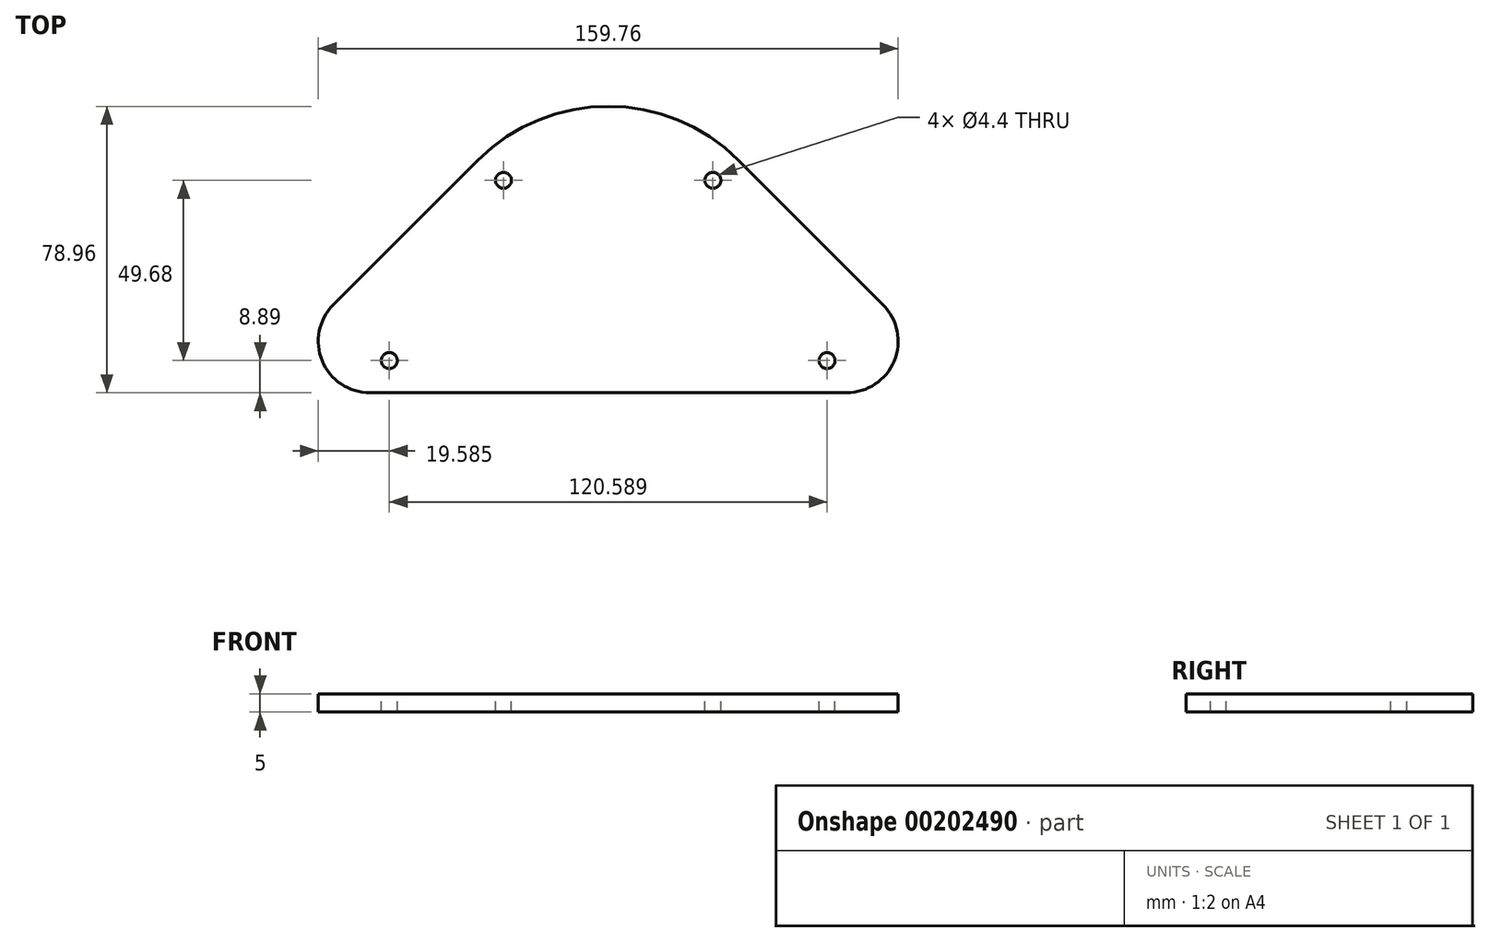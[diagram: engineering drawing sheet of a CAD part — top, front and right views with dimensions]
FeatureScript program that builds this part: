
annotation { "Feature Type Name" : "Feature", "Feature Type Description" : "" }
export const myFeature = defineFeature(function(context is Context, id is Id, definition is map)
    precondition{}
    {
        {
            var Q0;
            Q0=qCreatedBy(makeId("Top.planeOp"),FACE);
            var sketch = newSketch(context, id + "F0", { "sketchPlane" : qUnion([Q0])});
            skLineSegment(sketch, "E0", {"start": v(-100, 0) * mm, "end": v(0, 100) * mm});
            skLineSegment(sketch, "E1", {"start": v(0, 100) * mm, "end": v(100, 0) * mm});
            skLineSegment(sketch, "E2", {"start": v(100, 0) * mm, "end": v(-100, 0) * mm});
            skSolve(sketch);
        }
        {
            var Q0;
            Q0 = qSketchRegion(id + "F0", true);
            extrude(context, id + "F1", {"entities" : qUnion([Q0]), "depth" : 5 * mm});
        }
        {
            var Q0;
            Q0=makeQuery(id+"F1.opExtrude","SWEPT_EDGE",EDGE,{"disambiguationData":[OSD([sQuery(id+"F0.wireOp",EDGE,"E0"),sQuery(id+"F0.wireOp",EDGE,"E1")])]});
            fillet(context, id + "F2", {"entities" : qUnion([Q0]), "radius" : 50.8 * mm, "tangentPropagation" : true, "allowEdgeOverflow" : false});
        }
        {
            var Q0;
            Q0=makeQuery(id+"F1.opExtrude","SWEPT_EDGE",EDGE,{"disambiguationData":[OSD([sQuery(id+"F0.wireOp",EDGE,"E0"),sQuery(id+"F0.wireOp",EDGE,"E2")])]});
            var Q1;
            Q1=makeQuery(id+"F1.opExtrude","SWEPT_EDGE",EDGE,{"disambiguationData":[OSD([sQuery(id+"F0.wireOp",EDGE,"E1"),sQuery(id+"F0.wireOp",EDGE,"E2")])]});
            fillet(context, id + "F3", {"entities" : qUnion([Q0, Q1]), "radius" : 14.22 * mm, "tangentPropagation" : true, "allowEdgeOverflow" : false});
        }
        {
            var Q0;
            Q0=makeQuery(id+"F1.opExtrude","CAP_FACE",FACE,{"disambiguationData":[OSD([sQuery(id+"F0.wireOp",EDGE,"E0"),sQuery(id+"F0.wireOp",EDGE,"E1"),sQuery(id+"F0.wireOp",EDGE,"E2")])],"isStart":false});
            var sketch = newSketch(context, id + "F4", { "sketchPlane" : qUnion([Q0])});
            skLineSegment(sketch, "E3", {"start": v(-60.3, 8.89) * mm, "end": v(60.3, 8.89) * mm, "construction": true});
            skLineSegment(sketch, "E4", {"start": v(-28.86, 58.57) * mm, "end": v(28.86, 58.57) * mm, "construction": true});
            skPoint(sketch, "E5", {"position": v(0, 8.89) * mm});
            skPoint(sketch, "E6", {"position": v(0, 58.57) * mm});
            skSolve(sketch);
        }
        {
            var Q0;
            Q0=sQuery(id+"F4.wireOp",VERTEX,"E4.start");
            var Q1;
            Q1=sQuery(id+"F4.wireOp",VERTEX,"E4.end");
            var Q2;
            Q2=sQuery(id+"F4.wireOp",VERTEX,"E3.end");
            var Q3;
            Q3=sQuery(id+"F4.wireOp",VERTEX,"E3.start");
            var Q4;
            Q4=makeQuery(id+"F1.opExtrude","SWEPT_BODY",BODY,{"disambiguationData":[OSD([sQuery(id+"F0.wireOp",EDGE,"E0"),sQuery(id+"F0.wireOp",EDGE,"E1"),sQuery(id+"F0.wireOp",EDGE,"E2")])]});
            hole(context, id + "F5", {"style" : HoleStyle.SIMPLE, "endStyle" : HoleEndStyle.THROUGH, "standardTappedOrClearance" : lookupTablePath({ "standard" : "ISO", "fit" : "Normal", "size" : "M4", "type" : "Clearance" }), "standardBlindInLast" : lookupTablePath({ "fit" : "Standard", "standard" : "ISO", "size" : "M4", "type" : "Clearance" }), "holeDiameter" : 4.4 * mm, "locations" : qUnion([Q0, Q1, Q2, Q3]), "scope" : qUnion([Q4]), "isTappedThrough" : true});
        }
    });
